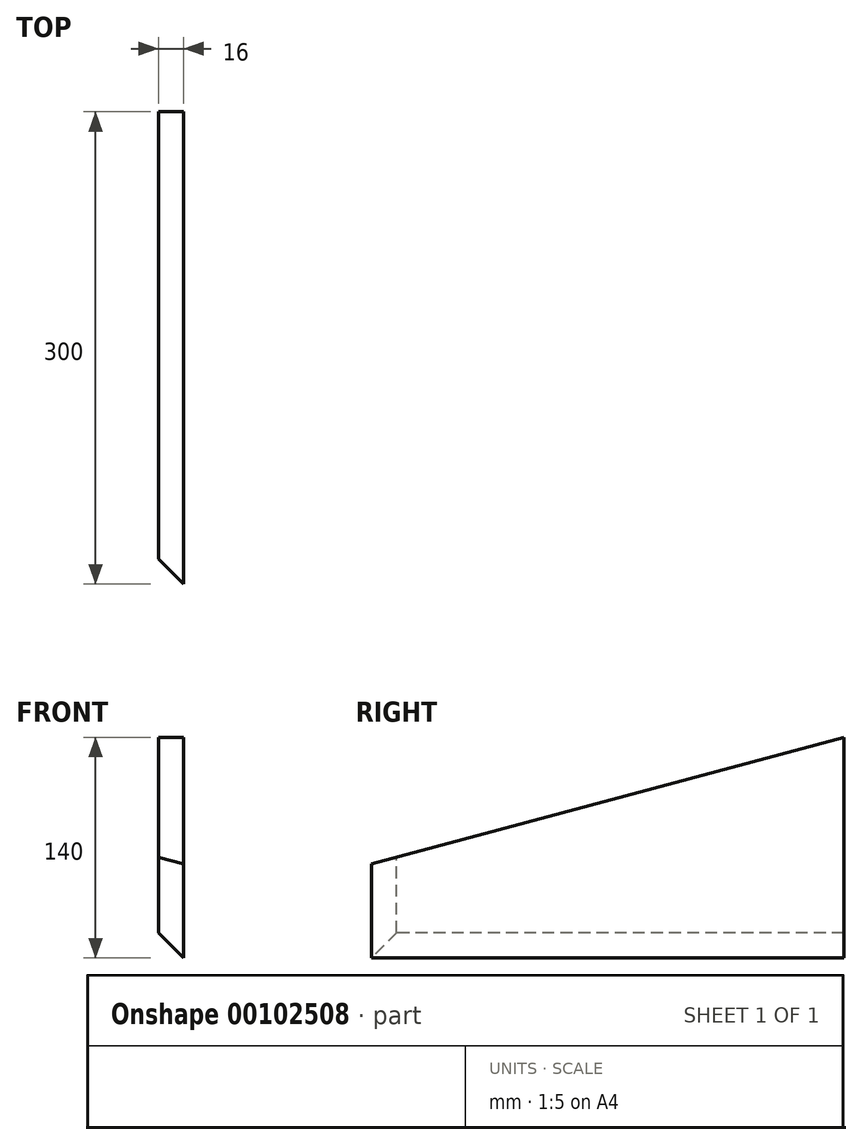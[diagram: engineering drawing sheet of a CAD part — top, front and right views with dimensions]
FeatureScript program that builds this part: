
annotation { "Feature Type Name" : "Feature", "Feature Type Description" : "" }
export const myFeature = defineFeature(function(context is Context, id is Id, definition is map)
    precondition{}
    {
        {
            var Q0;
            Q0=qCreatedBy(makeId("Right.planeOp"),FACE);
            var sketch = newSketch(context, id + "F0", { "sketchPlane" : qUnion([Q0])});
            skLineSegment(sketch, "E0", {"start": v(0, 0) * mm, "end": v(300, 0) * mm});
            skLineSegment(sketch, "E1", {"start": v(300, 0) * mm, "end": v(300, 140) * mm});
            skLineSegment(sketch, "E2", {"start": v(300, 140) * mm, "end": v(0, 59.62) * mm});
            skLineSegment(sketch, "E3", {"start": v(0, 59.62) * mm, "end": v(0, 0) * mm});
            skSolve(sketch);
        }
        {
            var Q0;
            Q0 = qSketchRegion(id + "F0", true);
            extrude(context, id + "F1", {"entities" : qUnion([Q0]), "depth" : 16 * mm});
        }
        {
            var Q0;
            Q0=makeQuery(id+"F1.opExtrude","CAP_EDGE",EDGE,{"disambiguationData":[OSD([sQuery(id+"F0.wireOp",EDGE,"E3")])],"isStart":true});
            var Q1;
            Q1=makeQuery(id+"F1.opExtrude","CAP_EDGE",EDGE,{"disambiguationData":[OSD([sQuery(id+"F0.wireOp",EDGE,"E0")])],"isStart":true});
            chamfer(context, id + "F2", {"entities" : qUnion([Q0, Q1]), "width" : 16 * mm, "tangentPropagation" : true});
        }
    });
